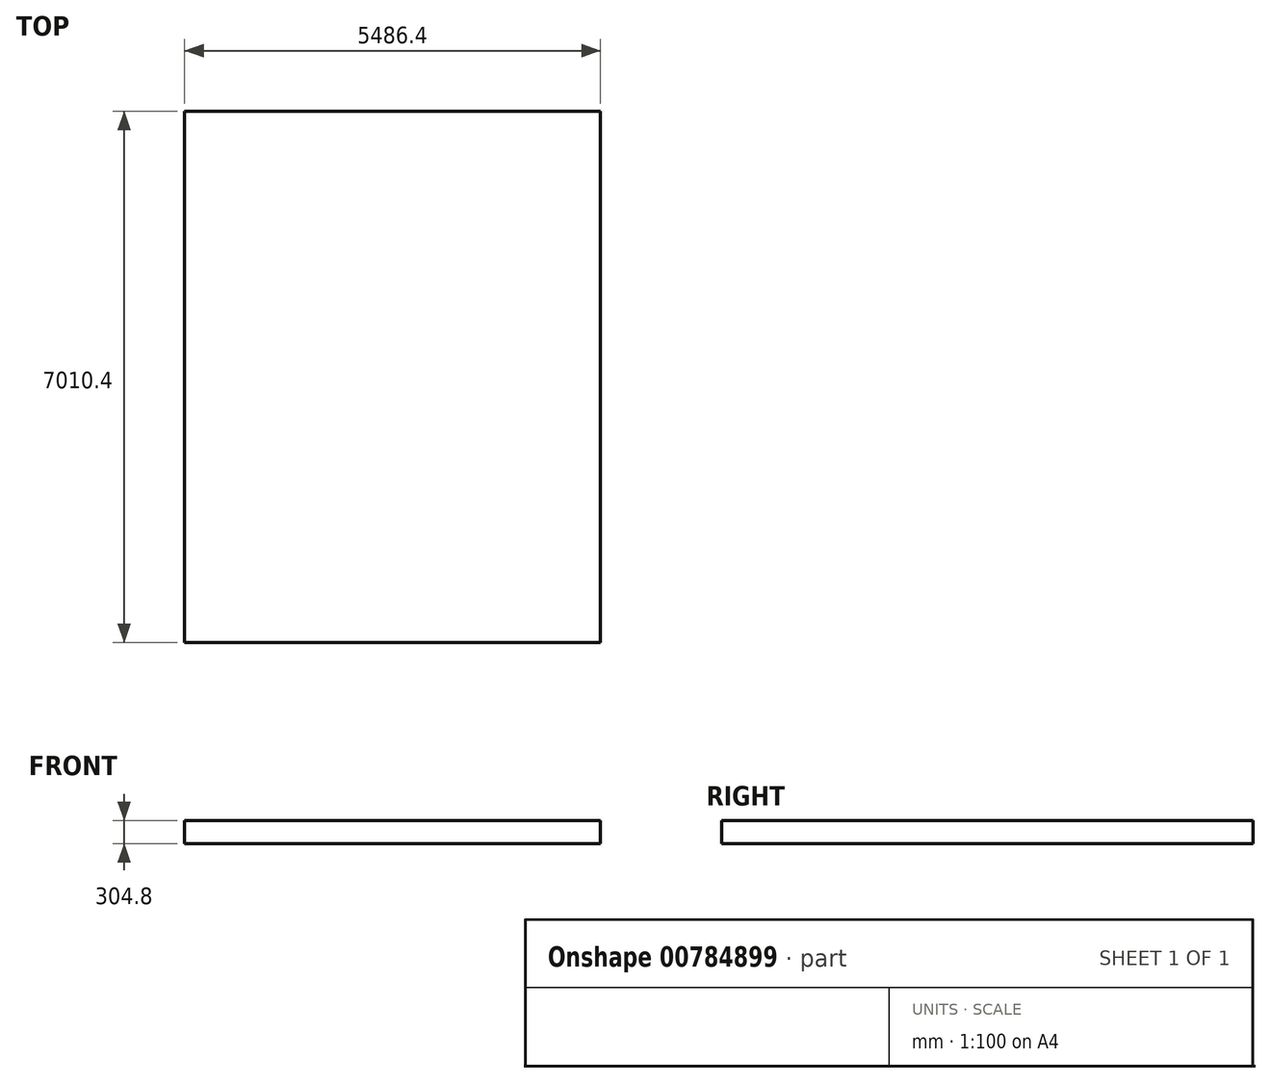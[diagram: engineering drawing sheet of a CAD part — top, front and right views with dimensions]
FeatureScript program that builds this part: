
annotation { "Feature Type Name" : "Feature", "Feature Type Description" : "" }
export const myFeature = defineFeature(function(context is Context, id is Id, definition is map)
    precondition{}
    {
        {
            var Q0;
            Q0=qCreatedBy(makeId("Top.planeOp"),FACE);
            var sketch = newSketch(context, id + "F0", { "sketchPlane" : qUnion([Q0])});
            skLineSegment(sketch, "E0.bottom", {"start": v(2743.2, 3505.2) * mm, "end": v(-2743.2, 3505.2) * mm});
            skLineSegment(sketch, "E0.top", {"start": v(2743.2, -3505.2) * mm, "end": v(-2743.2, -3505.2) * mm});
            skLineSegment(sketch, "E0.left", {"start": v(2743.2, 3505.2) * mm, "end": v(2743.2, -3505.2) * mm});
            skLineSegment(sketch, "E0.right", {"start": v(-2743.2, 3505.2) * mm, "end": v(-2743.2, -3505.2) * mm});
            skPoint(sketch, "E0.middle", {"position": v(0, 0) * mm});
            skSolve(sketch);
        }
        {
            var Q0;
            Q0=makeQuery(id+"F0.imprint","IMPRINT",FACE,{"disambiguationData":[TD([[makeQuery(id+"F0.imprint","IMPRINT",EDGE,{"derivedFrom":sQuery(id+"F0.wireOp",EDGE,"E0.bottom")}),1.0]])]});
            extrude(context, id + "F1", {"entities" : qUnion([Q0]), "depth" : 304.8 * mm, "offsetDistance" : 25.4 * mm});
        }
    });
